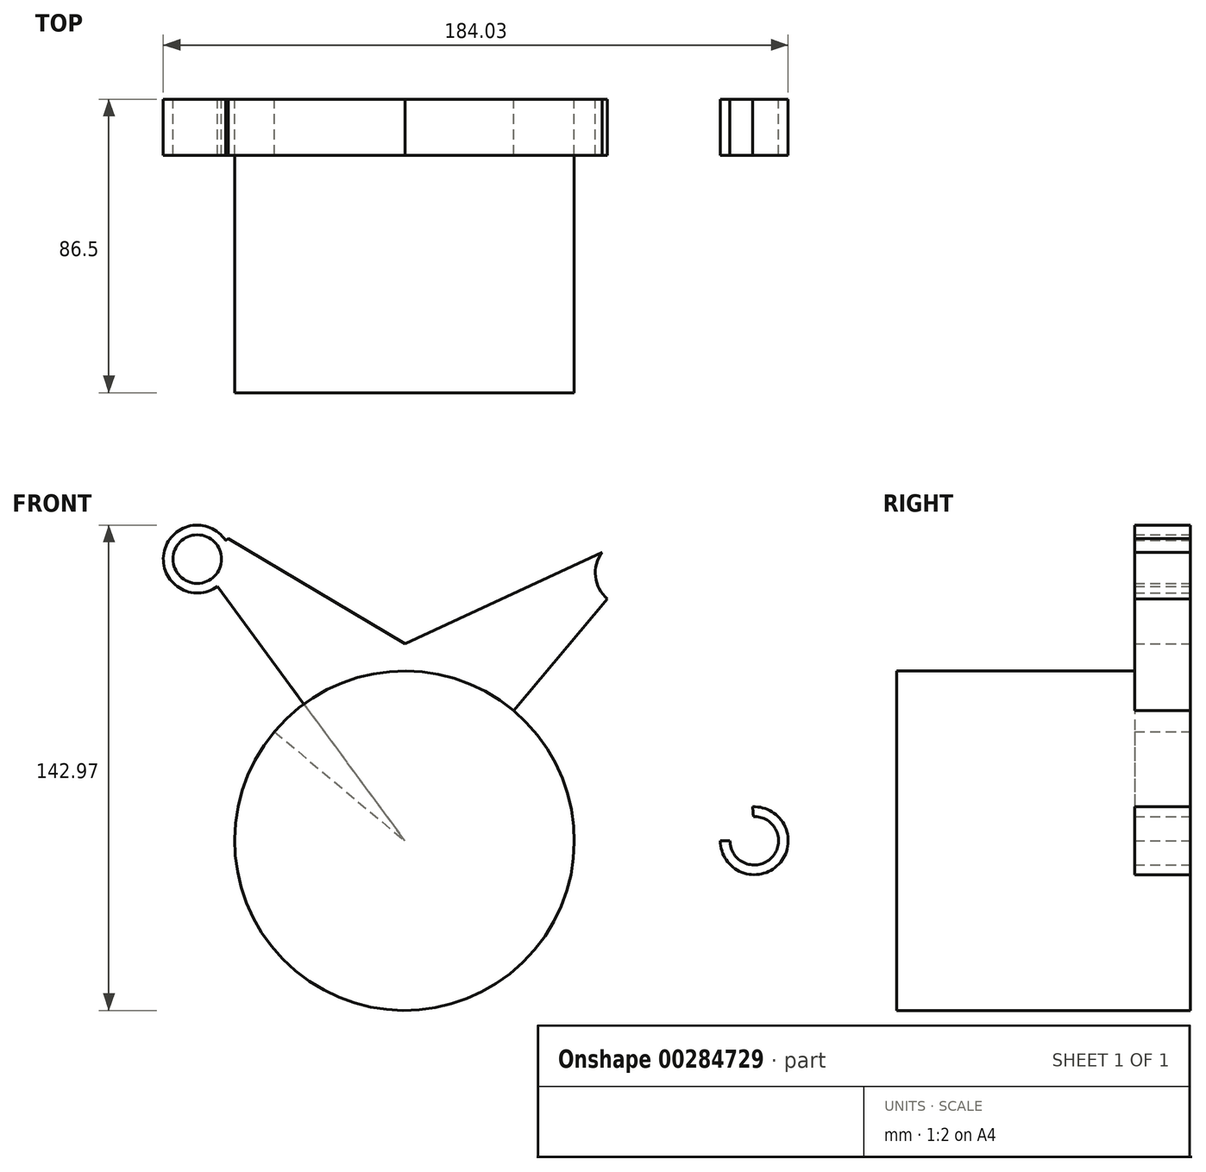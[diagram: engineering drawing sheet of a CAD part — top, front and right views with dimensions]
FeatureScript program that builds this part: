
annotation { "Feature Type Name" : "Feature", "Feature Type Description" : "" }
export const myFeature = defineFeature(function(context is Context, id is Id, definition is map)
    precondition{}
    {
        {
            var Q0;
            Q0=qCreatedBy(makeId("Front.planeOp"),FACE);
            var sketch = newSketch(context, id + "F0", { "sketchPlane" : qUnion([Q0])});
            skCircle(sketch, "E0", {"center": v(0, 0) * mm, "radius": 50 * mm});
            skCircle(sketch, "E1", {"center": v(0, 0) * mm, "radius": 103 * mm});
            skPoint(sketch, "E2", {"position": v(24.33, 100.08) * mm});
            skPoint(sketch, "E3", {"position": v(103, 0) * mm});
            skCircle(sketch, "E4", {"center": v(24.33, 100.08) * mm, "radius": 7.15 * mm});
            skCircle(sketch, "E5", {"center": v(103, 0) * mm, "radius": 7.15 * mm});
            skLineSegment(sketch, "E6", {"start": v(24.33, 100.08) * mm, "end": v(0, 0) * mm});
            skLineSegment(sketch, "E7", {"start": v(0, 0) * mm, "end": v(103, 0) * mm});
            skLineSegment(sketch, "E8", {"start": v(0, 50) * mm, "end": v(0, -50) * mm});
            skCircle(sketch, "E9", {"center": v(24.33, 100.08) * mm, "radius": 10 * mm});
            skCircle(sketch, "E10", {"center": v(103, 0) * mm, "radius": 10 * mm});
            skPoint(sketch, "E11", {"position": v(34.33, 100.08) * mm});
            skPoint(sketch, "E12", {"position": v(102.67, 8.28) * mm});
            skLineSegment(sketch, "E13", {"start": v(34.33, 100.08) * mm, "end": v(44.6, 37.18) * mm});
            skLineSegment(sketch, "E14", {"start": v(44.6, 37.18) * mm, "end": v(102.51, 9.99) * mm});
            skSolve(sketch);
        }
        {
            var Q0;
            {var subQ0=sQuery(id+"F0.wireOp",EDGE,"E6");var subQ1=sQuery(id+"F0.wireOp",EDGE,"E0");var subQ2=makeQuery(id+"F0.imprint","INTERSECT",VERTEX,{"derivedFrom":[subQ1,subQ0]});Q0=makeQuery(id+"F0.imprint","IMPRINT",FACE,{"disambiguationData":[TD([[makeQuery(id+"F0.imprint","IMPRINT",EDGE,{"disambiguationData":[TD([[subQ2,1.0]])],"derivedFrom":subQ1}),1.0]])]});}
            var Q1;
            {var subQ13=sQuery(id+"F0.wireOp",EDGE,"E14");Q1=makeQuery(id+"F0.imprint","IMPRINT",FACE,{"disambiguationData":[TD([[makeQuery(id+"F0.imprint","IMPRINT",EDGE,{"derivedFrom":subQ13}),-1.0]])]});}
            var Q2;
            {var subQ0=sQuery(id+"F0.wireOp",EDGE,"E10");var subQ1=sQuery(id+"F0.wireOp",EDGE,"E1");var subQ6=makeQuery(id+"F0.imprint","INTERSECT",VERTEX,{"derivedFrom":[subQ1,subQ0]});Q2=makeQuery(id+"F0.imprint","IMPRINT",FACE,{"disambiguationData":[TD([[makeQuery(id+"F0.imprint","IMPRINT",EDGE,{"disambiguationData":[TD([[subQ6,-1.0]])],"derivedFrom":subQ1}),-1.0]])]});}
            var Q3;
            {var subQ0=sQuery(id+"F0.wireOp",EDGE,"E10");var subQ1=sQuery(id+"F0.wireOp",EDGE,"E1");var subQ2=makeQuery(id+"F0.imprint","INTERSECT",VERTEX,{"derivedFrom":[subQ1,subQ0]});Q3=makeQuery(id+"F0.imprint","IMPRINT",FACE,{"disambiguationData":[TD([[makeQuery(id+"F0.imprint","IMPRINT",EDGE,{"disambiguationData":[TD([[subQ2,-1.0]])],"derivedFrom":subQ1}),1.0]])]});}
            var Q4;
            {var subQ1=sQuery(id+"F0.wireOp",EDGE,"E1");var subQ3=sQuery(id+"F0.wireOp",EDGE,"E5");var subQ4=makeQuery(id+"F0.imprint","INTERSECT",VERTEX,{"disambiguationData":[OD(0.0)],"derivedFrom":[subQ1,subQ3]});Q4=makeQuery(id+"F0.imprint","IMPRINT",FACE,{"disambiguationData":[TD([[makeQuery(id+"F0.imprint","IMPRINT",EDGE,{"disambiguationData":[TD([[subQ4,-1.0]])],"derivedFrom":subQ3}),-1.0]])]});}
            var Q5;
            {var subQ1=sQuery(id+"F0.wireOp",EDGE,"E1");var subQ4=sQuery(id+"F0.wireOp",EDGE,"E9");var subQ7=makeQuery(id+"F0.imprint","INTERSECT",VERTEX,{"disambiguationData":[OD(1.0)],"derivedFrom":[subQ1,subQ4]});Q5=makeQuery(id+"F0.imprint","IMPRINT",FACE,{"disambiguationData":[TD([[makeQuery(id+"F0.imprint","IMPRINT",EDGE,{"disambiguationData":[TD([[subQ7,-1.0]])],"derivedFrom":subQ1}),-1.0]])]});}
            var Q6;
            {var subQ0=sQuery(id+"F0.wireOp",EDGE,"E9");var subQ1=sQuery(id+"F0.wireOp",EDGE,"E1");var subQ2=makeQuery(id+"F0.imprint","INTERSECT",VERTEX,{"disambiguationData":[OD(1.0)],"derivedFrom":[subQ1,subQ0]});Q6=makeQuery(id+"F0.imprint","IMPRINT",FACE,{"disambiguationData":[TD([[makeQuery(id+"F0.imprint","IMPRINT",EDGE,{"disambiguationData":[TD([[subQ2,-1.0]])],"derivedFrom":subQ1}),1.0]])]});}
            var Q7;
            {var subQ0=sQuery(id+"F0.wireOp",EDGE,"E9");var subQ1=sQuery(id+"F0.wireOp",EDGE,"E1");var subQ2=makeQuery(id+"F0.imprint","INTERSECT",VERTEX,{"disambiguationData":[OD(0.0)],"derivedFrom":[subQ1,subQ0]});Q7=makeQuery(id+"F0.imprint","IMPRINT",FACE,{"disambiguationData":[TD([[makeQuery(id+"F0.imprint","IMPRINT",EDGE,{"disambiguationData":[TD([[subQ2,1.0]])],"derivedFrom":subQ1}),1.0]])]});}
            var Q8;
            {var subQ0=sQuery(id+"F0.wireOp",EDGE,"E8");var subQ1=sQuery(id+"F0.wireOp",EDGE,"E0");var subQ2=makeQuery(id+"F0.imprint","INTERSECT",VERTEX,{"disambiguationData":[OD(0.0)],"derivedFrom":[subQ1,subQ0]});Q8=makeQuery(id+"F0.imprint","IMPRINT",FACE,{"disambiguationData":[TD([[makeQuery(id+"F0.imprint","IMPRINT",EDGE,{"disambiguationData":[TD([[subQ2,-1.0]])],"derivedFrom":subQ1}),1.0]])]});}
            var Q9;
            {var subQ0=sQuery(id+"F0.wireOp",EDGE,"E8");var subQ1=sQuery(id+"F0.wireOp",EDGE,"E0");var subQ2=makeQuery(id+"F0.imprint","INTERSECT",VERTEX,{"disambiguationData":[OD(1.0)],"derivedFrom":[subQ1,subQ0]});Q9=makeQuery(id+"F0.imprint","IMPRINT",FACE,{"disambiguationData":[TD([[makeQuery(id+"F0.imprint","IMPRINT",EDGE,{"disambiguationData":[TD([[subQ2,-1.0]])],"derivedFrom":subQ1}),1.0]])]});}
            var Q10;
            {var subQ0=sQuery(id+"F0.wireOp",EDGE,"E8");var subQ1=sQuery(id+"F0.wireOp",EDGE,"E0");var subQ2=makeQuery(id+"F0.imprint","INTERSECT",VERTEX,{"disambiguationData":[OD(0.0)],"derivedFrom":[subQ1,subQ0]});Q10=makeQuery(id+"F0.imprint","IMPRINT",FACE,{"disambiguationData":[TD([[makeQuery(id+"F0.imprint","IMPRINT",EDGE,{"disambiguationData":[TD([[subQ2,1.0]])],"derivedFrom":subQ1}),1.0]])]});}
            extrude(context, id + "F1", {"entities" : qUnion([Q0, Q1, Q2, Q3, Q4, Q5, Q6, Q7, Q8, Q9, Q10]), "depth" : 16.5 * mm});
        }
        {
            var Q0;
            Q0=makeQuery(id+"F1.opExtrude","CAP_FACE",FACE,{"disambiguationData":[OSD([sQuery(id+"F0.wireOp",EDGE,"E0"),sQuery(id+"F0.wireOp",EDGE,"E1"),sQuery(id+"F0.wireOp",EDGE,"E4"),sQuery(id+"F0.wireOp",EDGE,"E5"),sQuery(id+"F0.wireOp",EDGE,"E6"),sQuery(id+"F0.wireOp",EDGE,"E7"),sQuery(id+"F0.wireOp",EDGE,"E9"),sQuery(id+"F0.wireOp",EDGE,"E10"),sQuery(id+"F0.wireOp",EDGE,"E13"),sQuery(id+"F0.wireOp",EDGE,"E14")])],"isStart":false});
            var sketch = newSketch(context, id + "F2", { "sketchPlane" : qUnion([Q0])});
            skArc(sketch, "E15.0", {"start": v(11.81, 48.58) * mm, "mid": v(-39.31, -30.9) * mm, "end": v(50, 0) * mm});
            skCircle(sketch, "E16", {"center": v(0, 0) * mm, "radius": 50 * mm});
            skSolve(sketch);
        }
        {
            var Q0;
            Q0 = qSketchRegion(id + "F2", true);
            extrude(context, id + "F3", {"entities" : qUnion([Q0]), "operationType" : NewBodyOperationType.ADD, "depth" : 70 * mm});
        }
        {
            var Q0;
            Q0=makeQuery(id+"F1.opExtrude","SWEPT_BODY",BODY,{"disambiguationData":[OSD([sQuery(id+"F0.wireOp",EDGE,"E0"),sQuery(id+"F0.wireOp",EDGE,"E1"),sQuery(id+"F0.wireOp",EDGE,"E4"),sQuery(id+"F0.wireOp",EDGE,"E5"),sQuery(id+"F0.wireOp",EDGE,"E6"),sQuery(id+"F0.wireOp",EDGE,"E7"),sQuery(id+"F0.wireOp",EDGE,"E9"),sQuery(id+"F0.wireOp",EDGE,"E10"),sQuery(id+"F0.wireOp",EDGE,"E13"),sQuery(id+"F0.wireOp",EDGE,"E14")])]});
            var Q1;
            Q1=makeQuery(id+"F3.opExtrude","CAP_EDGE",EDGE,{"disambiguationData":[OSD([sQuery(id+"F2.wireOp",EDGE,"E16")])],"isStart":false});
            transform(context, id + "F4", {"entities" : qUnion([Q0]), "transformType" : TransformType.ROTATION, "transformAxis" : qUnion([Q1]), "angle" : 50 * degree, "makeCopy" : false});
        }
    });
